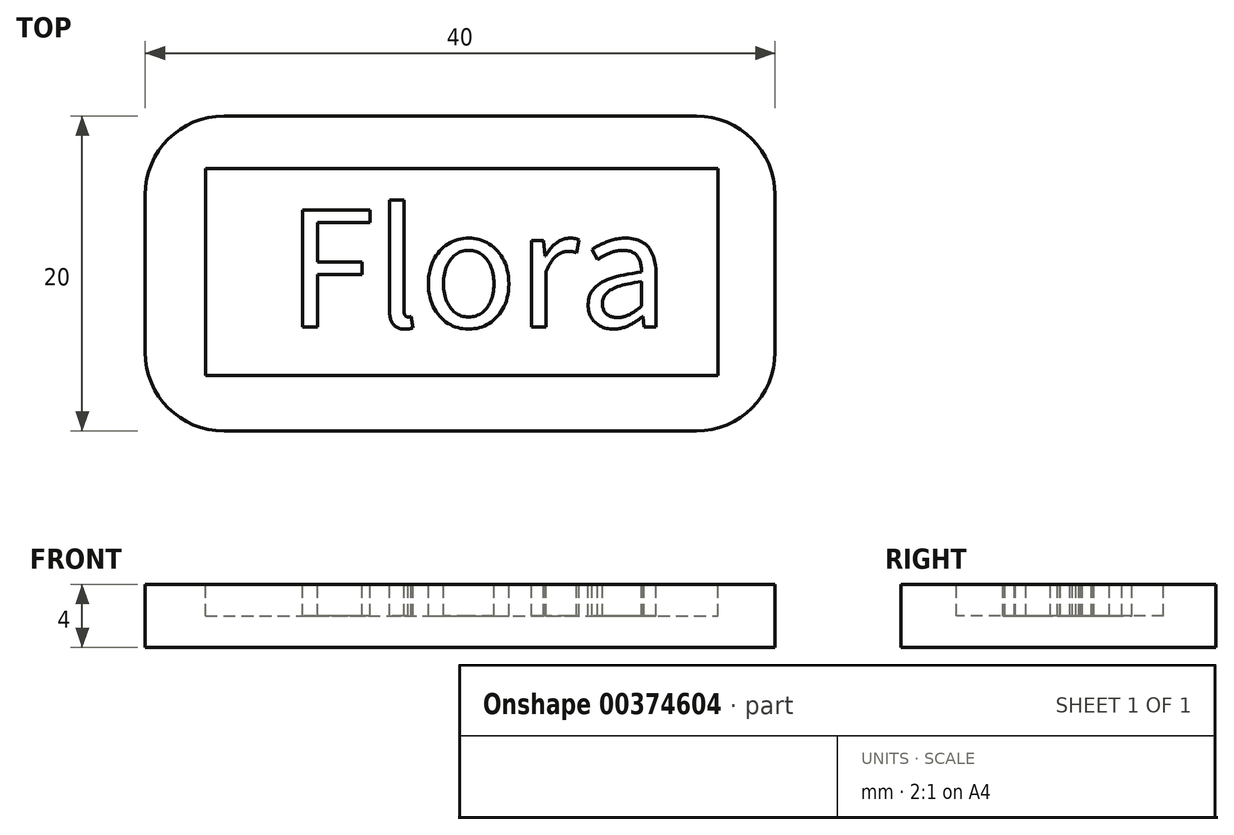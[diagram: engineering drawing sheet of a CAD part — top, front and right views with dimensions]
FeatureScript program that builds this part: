
annotation { "Feature Type Name" : "Feature", "Feature Type Description" : "" }
export const myFeature = defineFeature(function(context is Context, id is Id, definition is map)
    precondition{}
    {
        {
            var Q0;
            Q0=qCreatedBy(makeId("Top.planeOp"),FACE);
            var sketch = newSketch(context, id + "F0", { "sketchPlane" : qUnion([Q0])});
            skLineSegment(sketch, "E0.bottom", {"start": v(-15, 10) * mm, "end": v(15, 10) * mm});
            skLineSegment(sketch, "E0.top", {"start": v(-15, -10) * mm, "end": v(15, -10) * mm});
            skLineSegment(sketch, "E0.left", {"start": v(-20, 5) * mm, "end": v(-20, -5) * mm});
            skLineSegment(sketch, "E0.right", {"start": v(20, 5) * mm, "end": v(20, -5) * mm});
            skPoint(sketch, "E0.middle", {"position": v(0, 0) * mm});
            skPoint(sketch, "E1.visualSharp", {"position": v(-20, 10) * mm});
            skArc(sketch, "E1.filletArc", {"start": v(-15, 10) * mm, "mid": v(-18.54, 8.54) * mm, "end": v(-20, 5) * mm});
            skPoint(sketch, "E2.visualSharp", {"position": v(20, 10) * mm});
            skArc(sketch, "E2.filletArc", {"start": v(20, 5) * mm, "mid": v(18.54, 8.54) * mm, "end": v(15, 10) * mm});
            skPoint(sketch, "E3.visualSharp", {"position": v(20, -10) * mm});
            skArc(sketch, "E3.filletArc", {"start": v(15, -10) * mm, "mid": v(18.54, -8.54) * mm, "end": v(20, -5) * mm});
            skPoint(sketch, "E4.visualSharp", {"position": v(-20, -10) * mm});
            skArc(sketch, "E4.filletArc", {"start": v(-20, -5) * mm, "mid": v(-18.54, -8.54) * mm, "end": v(-15, -10) * mm});
            skSolve(sketch);
        }
        {
            var Q0;
            Q0=makeQuery(id+"F0.imprint","IMPRINT",FACE,{"disambiguationData":[TD([[makeQuery(id+"F0.imprint","IMPRINT",EDGE,{"derivedFrom":sQuery(id+"F0.wireOp",EDGE,"E0.bottom")}),-1.0]])]});
            extrude(context, id + "F1", {"entities" : qUnion([Q0]), "depth" : 4 * mm});
        }
        {
            var Q0;
            Q0=makeQuery(id+"F1.opExtrude","CAP_FACE",FACE,{"disambiguationData":[OSD([sQuery(id+"F0.wireOp",EDGE,"E0.bottom"),sQuery(id+"F0.wireOp",EDGE,"E0.top"),sQuery(id+"F0.wireOp",EDGE,"E0.left"),sQuery(id+"F0.wireOp",EDGE,"E0.right"),sQuery(id+"F0.wireOp",EDGE,"E1.filletArc"),sQuery(id+"F0.wireOp",EDGE,"E2.filletArc"),sQuery(id+"F0.wireOp",EDGE,"E3.filletArc"),sQuery(id+"F0.wireOp",EDGE,"E4.filletArc")])],"isStart":false});
            var sketch = newSketch(context, id + "F2", { "sketchPlane" : qUnion([Q0])});
            skLineSegment(sketch, "E5.bottom", {"start": v(-16.18, 6.68) * mm, "end": v(16.37, 6.68) * mm});
            skLineSegment(sketch, "E5.top", {"start": v(-16.18, -6.5) * mm, "end": v(16.37, -6.5) * mm});
            skLineSegment(sketch, "E5.left", {"start": v(-16.18, 6.68) * mm, "end": v(-16.18, -6.5) * mm});
            skLineSegment(sketch, "E5.right", {"start": v(16.37, 6.68) * mm, "end": v(16.37, -6.5) * mm});
            skText(sketch, "E6", { "text": "Flora\n", "fontName": "NotoSansCJKtc-Regular.otf"});
            const initialGuessF2  = {"E6": [-0.01102, -0.0034, 1, 0, 0.0073]};
            skSetInitialGuess(sketch, initialGuessF2);
            skSolve(sketch);
        }
        {
            var Q0;
            Q0=makeQuery(id+"F2.imprint","IMPRINT",FACE,{"disambiguationData":[TD([[makeQuery(id+"F2.imprint","IMPRINT",EDGE,{"derivedFrom":sQuery(id+"F2.wireOp",EDGE,"E5.bottom")}),-1.0]])]});
            var Q1;
            Q1=makeQuery(id+"F2.imprint","IMPRINT",FACE,{"disambiguationData":[TD([[makeQuery(id+"F2.imprint","IMPRINT",EDGE,{"derivedFrom":sQuery(id+"F2.wireOp",EDGE,"E6.sketch_text.stroke-22")}),-1.0]])]});
            var Q2;
            Q2=makeQuery(id+"F2.imprint","IMPRINT",FACE,{"disambiguationData":[TD([[makeQuery(id+"F2.imprint","IMPRINT",EDGE,{"derivedFrom":sQuery(id+"F2.wireOp",EDGE,"E6.sketch_text.stroke-49")}),-1.0]])]});
            extrude(context, id + "F3", {"entities" : qUnion([Q0, Q1, Q2]), "operationType" : NewBodyOperationType.REMOVE, "oppositeDirection" : true, "depth" : 2 * mm});
        }
    });
